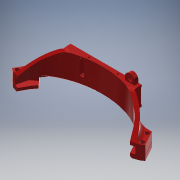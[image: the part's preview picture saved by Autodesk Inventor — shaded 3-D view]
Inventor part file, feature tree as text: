
AUTODESK INVENTOR PART (.ipt)
format: ipt  version: 2017 (Build 210142000, 142)  size: 587,264 bytes
history: native  units: mm
features: sketch x16, extrude x12, projected_geometry x11, other x9, reference x6, hole x5, chamfer x3, plane x3, mirror x2, fillet x2
ambient origin geometry x8: Origin, YZ Plane, XZ Plane, XY Plane, X Axis, Y Axis, Z Axis, Center Point
bodies: Body1 (feature_tree), Body2 (feature_tree), Body3 (feature_tree)
feature tree (69):
  other  "clamp_r"
  other  "core"
  extrude  "Extrusion1"  Depth=12.0mm
  extrude  "Extrusion2"  Depth=18.0mm
  extrude  "Extrusion3"  Depth=17.453293mm
  chamfer  "Chamfer1"  Distance=5.0mm
  hole  "Hole1"  [1 undecoded]
  hole  "Hole2"  [1 undecoded]
  plane  "Work Plane1"
  extrude  "Extrusion4"  Depth=4.0mm
  extrude  "Extrusion5"  Depth=24.0mm TaperAngle=0.0deg
  extrude  "Extrusion10"  Depth=158.0mm
  extrude  "Extrusion6"  Depth=1.8mm
  extrude  "Extrusion11"  Depth=59.5mm
  mirror  "Mirror1"
  hole  "Hole3"  [1 undecoded]
  plane  "Work Plane2"
  extrude  "Extrusion7"  Depth=4.0mm
  extrude  "Extrusion8"  Depth=8.6mm TaperAngle=0.0deg
  extrude  "Extrusion9"  Depth=2.0mm
  hole  "Hole4"  [1 undecoded]
  extrude  "Extrusion13"  Depth=0.5mm TaperAngle=0.0deg
  chamfer  "Chamfer4"  Distance=4.0mm
  plane  "Work Plane3"
  mirror  "Mirror2"
  hole  "Hole5"  [1 undecoded]
  fillet  "Fillet1"  Radius=16.0mm
  fillet  "Fillet2"  Radius=4.0mm
  chamfer  "Chamfer3"  Distance=30.0mm
  sketch  "Sketch1"  dims[d1=8.0mm d2=12.0mm]
  reference  "Reference1"
  reference  "Reference2"
  sketch  "Sketch2"  dims[d3=3.0mm d4=0.0mm d5=18.0mm]
  projected_geometry  "Projected Loop1"
  sketch  "Sketch3"  dims[d6=6.5mm d7=0.0mm d8=17.453293mm]
  projected_geometry  "Projected Loop2"
  sketch  "Sketch4"  dims[d9=16.0mm]
  projected_geometry  "Projected Loop3"
  sketch  "Sketch5"  dims[d10=6.0mm d11=5.0mm d12=0.0mm]
  sketch  "Sketch6"  dims[d13=1.5mm d14=2.0mm d15=45.0deg d19=12.0mm]
  reference  "Reference3"
  projected_geometry  "Projected Loop4"
  sketch  "Sketch7"  dims[d20=4.0mm d21=3.0mm]
  projected_geometry  "Projected Loop5"
  sketch  "Sketch8"  dims[d22=3.0mm]
  sketch  "Sketch9"  dims[d23=2.2mm d24=6.0mm d25=4.0mm d26=2.0mm d27=90.0deg d28=8.0mm d29=20.594885mm]
  projected_geometry  "Projected Loop6"
  sketch  "Sketch10"  dims[d30=2.2mm d31=6.0mm d32=4.0mm d33=2.0mm d34=90.0deg d35=8.0mm d36=20.594885mm d38=4.0mm]
  sketch  "Sketch11"  dims[d39=3.0mm d40=0.0mm d41=24.0mm d42=0.0mm]
  projected_geometry  "Projected Loop7"
  sketch  "Sketch12"  dims[d43=10.0mm d44=0.0mm d45=158.0mm]
  reference  "Reference4"
  reference  "Reference5"
  reference  "Reference6"
  sketch  "Sketch13"  dims[d46=16.0mm d47=1.8mm]
  projected_geometry  "Projected Loop8"
  other  "Pattern of core:1"
  other  "clamp_l"
  sketch  "Sketch14"  dims[d48=1.8mm d49=59.5mm]
  projected_geometry  "Projected Loop9"
  sketch  "Sketch15"  dims[d50=1.8mm d51=6.0mm d52=1.0mm d53=2.0mm d54=90.0deg d55=8.0mm d56=20.594885mm d57=-10.25mm]
  projected_geometry  "Projected Loop10"
  sketch  "Sketch17"  dims[d58=4.0mm d59=4.0mm d60=8.6mm d61=0.0mm d62=2.0mm d63=2.0mm d65=0.5mm d66=0.0mm d67=4.0mm d68=0.0mm d69=10.0mm d70=10.0mm d71=2.2mm d72=6.0mm d73=4.5mm d74=1.5mm d75=90.0deg d76=8.0mm d77=20.594885mm d78=16.0mm d79=4.0mm d80=0.0mm d81=30.0mm d82=1.8mm d83=6.0mm d84=4.0mm d85=2.0mm d86=90.0deg d87=8.0mm d88=20.594885mm d89=4.05mm d90=4.05mm d91=4.0mm d92=0.0mm d93=12.0mm d94=4.0mm d95=2.0mm d96=2.0mm d97=45.0deg d100=0.65mm d101=0.0mm d102=1.2mm d103=2.0mm d104=45.0deg]
  projected_geometry  "Projected Loop12"
  other  "<userpath>\Dropbox\Work\HeadSLAM\xtion_custom_assembly.iam"
  other  "xtion_custom_assembly.iam"
  other  "pupil_frame_full:1"
  other  "xtion_custom:1"
  other  "<userpath>\Dropbox\Work\HeadSLAM\xtion_custom_assembly.iam"
note: 5 required parameter values undecoded (feature->parameter linkage not recoverable at this tier; creation-order binding heuristic only, values carry confidence <= 0.55)
